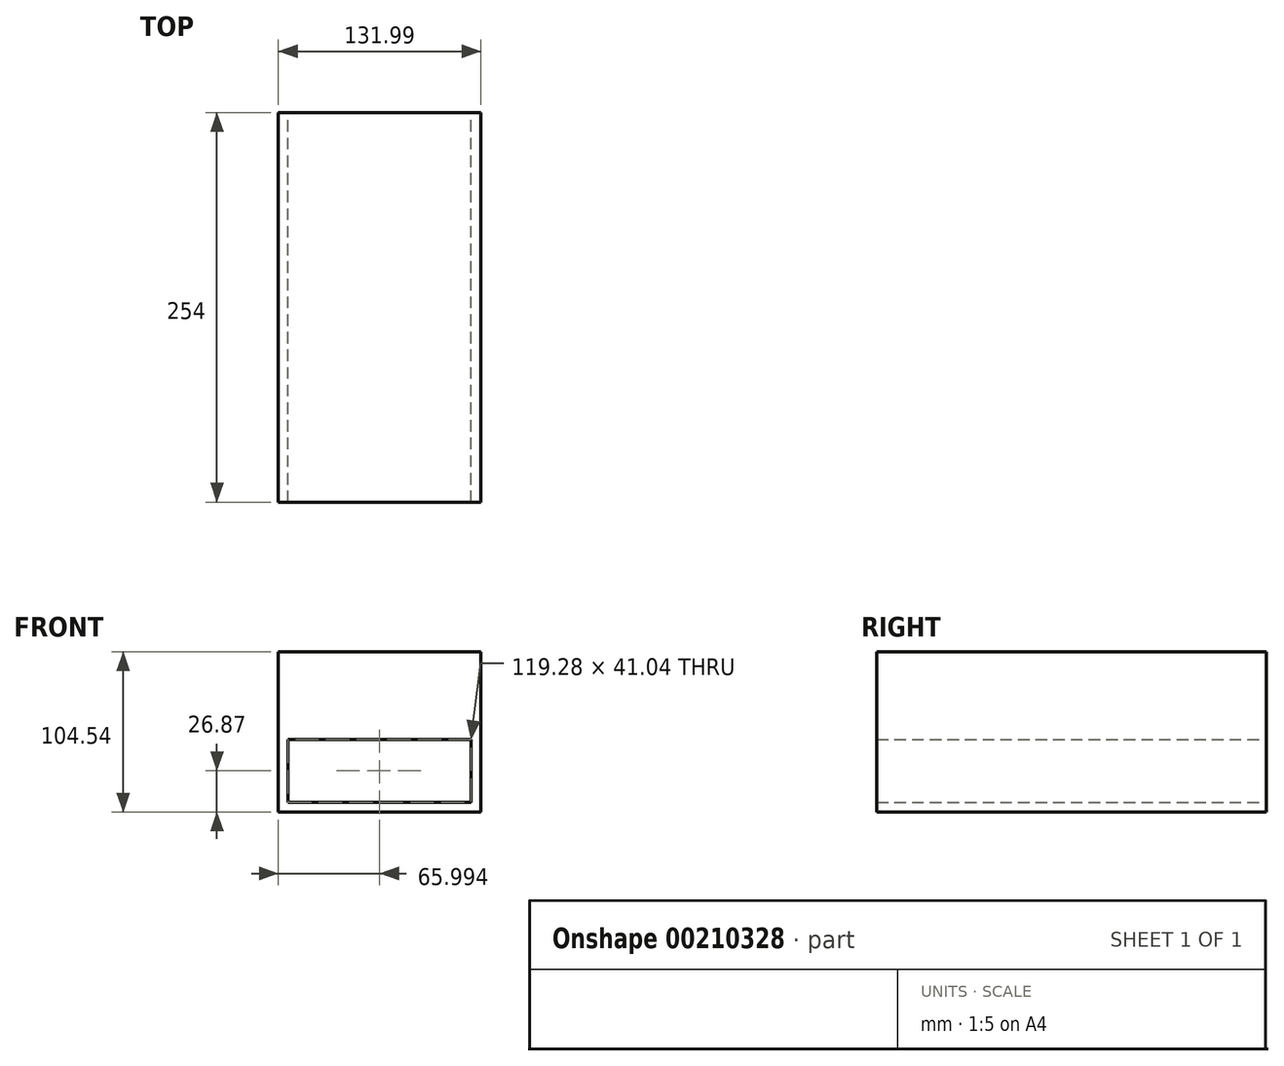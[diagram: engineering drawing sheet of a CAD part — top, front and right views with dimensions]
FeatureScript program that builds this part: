
annotation { "Feature Type Name" : "Feature", "Feature Type Description" : "" }
export const myFeature = defineFeature(function(context is Context, id is Id, definition is map)
    precondition{}
    {
        {
            var Q0;
            Q0=qCreatedBy(makeId("Front.planeOp"),FACE);
            var sketch = newSketch(context, id + "F0", { "sketchPlane" : qUnion([Q0])});
            skLineSegment(sketch, "E0.bottom", {"start": v(-58.94, 36.75) * mm, "end": v(73.05, 36.75) * mm});
            skLineSegment(sketch, "E0.top", {"start": v(-58.94, -67.8) * mm, "end": v(73.05, -67.8) * mm});
            skLineSegment(sketch, "E0.left", {"start": v(-58.94, 36.75) * mm, "end": v(-58.94, -67.8) * mm});
            skLineSegment(sketch, "E0.right", {"start": v(73.05, 36.75) * mm, "end": v(73.05, -67.8) * mm});
            skLineSegment(sketch, "E1.0", {"start": v(-52.59, 30.4) * mm, "end": v(66.7, 30.4) * mm});
            skLineSegment(sketch, "E2.0", {"start": v(66.7, 30.4) * mm, "end": v(66.7, -61.44) * mm});
            skLineSegment(sketch, "E3.0", {"start": v(-52.59, -61.44) * mm, "end": v(66.7, -61.44) * mm});
            skLineSegment(sketch, "E3.1", {"start": v(-52.59, 30.4) * mm, "end": v(-52.59, -61.44) * mm});
            skSolve(sketch);
        }
        {
            var Q0;
            Q0 = qSketchRegion(id + "F0", true);
            extrude(context, id + "F1", {"entities" : qUnion([Q0]), "depth" : 254 * mm, "symmetric" : true});
        }
        {
            var Q0;
            Q0=makeQuery(id+"F1.opExtrude","SWEPT_FACE",FACE,{"disambiguationData":[OSD([sQuery(id+"F0.wireOp",EDGE,"E1.0")])]});
            extrude(context, id + "F2", {"entities" : qUnion([Q0]), "operationType" : NewBodyOperationType.ADD, "depth" : 50.8 * mm});
        }
    });
